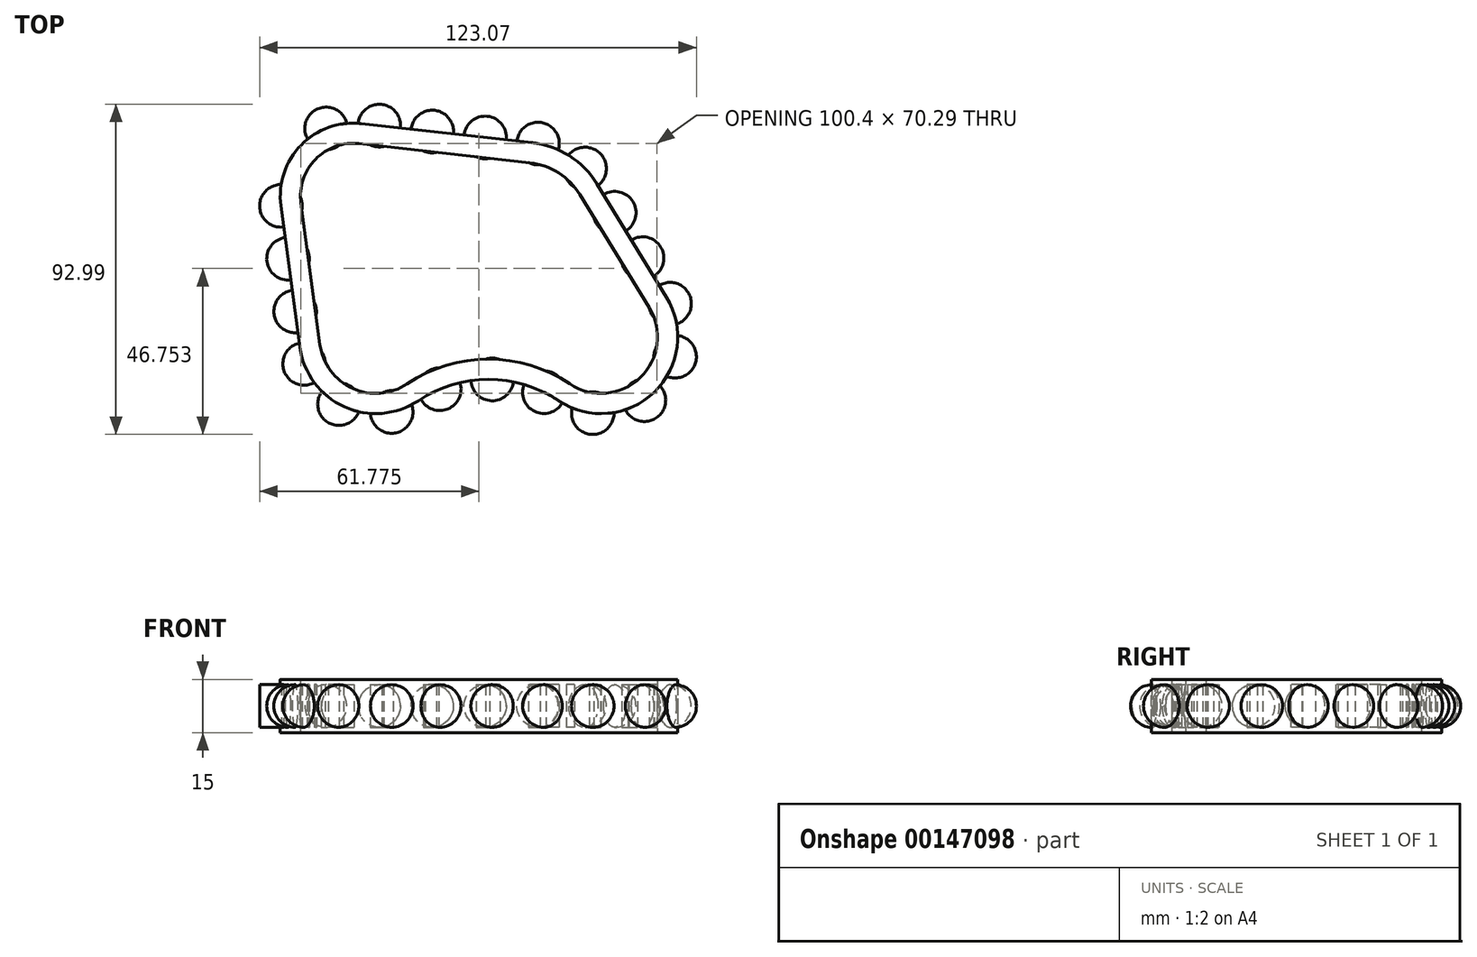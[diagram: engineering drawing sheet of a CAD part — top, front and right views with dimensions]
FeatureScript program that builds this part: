
annotation { "Feature Type Name" : "Feature", "Feature Type Description" : "" }
export const myFeature = defineFeature(function(context is Context, id is Id, definition is map)
    precondition{}
    {
        {
            var Q0;
            Q0=qCreatedBy(makeId("Top.planeOp"),FACE);
            var sketch = newSketch(context, id + "F0", { "sketchPlane" : qUnion([Q0])});
            skArc(sketch, "E0", {"start": v(-47.48, -2.12) * mm, "mid": v(-38.28, -14.47) * mm, "end": v(-22.93, -13.2) * mm});
            skArc(sketch, "E1", {"start": v(22.93, -13.2) * mm, "mid": v(42.76, -11.44) * mm, "end": v(45.28, 8.3) * mm});
            skLineSegment(sketch, "E2", {"start": v(-31.75, 0) * mm, "end": v(0, 0) * mm, "construction": true});
            skLineSegment(sketch, "E3", {"start": v(0, 0) * mm, "end": v(31.75, 0) * mm, "construction": true});
            skCircle(sketch, "E4", {"center": v(-38.1, 39.69) * mm, "radius": 15.91 * mm, "construction": true});
            skLineSegment(sketch, "E5", {"start": v(-38.1, 39.69) * mm, "end": v(0, 39.69) * mm, "construction": true});
            skLineSegment(sketch, "E6", {"start": v(0, 39.69) * mm, "end": v(0, 0) * mm, "construction": true});
            skArc(sketch, "E7.0", {"start": v(-53.12, -2.87) * mm, "mid": v(-40.62, -19.65) * mm, "end": v(-19.77, -17.93) * mm});
            skArc(sketch, "E8.0", {"start": v(19.77, -17.93) * mm, "mid": v(46.7, -15.54) * mm, "end": v(50.13, 11.27) * mm});
            skArc(sketch, "E9", {"start": v(22.93, -13.2) * mm, "mid": v(0, -6.24) * mm, "end": v(-22.93, -13.2) * mm});
            skArc(sketch, "E10", {"start": v(19.77, -17.93) * mm, "mid": v(0, -11.93) * mm, "end": v(-19.77, -17.93) * mm});
            skArc(sketch, "E11.0", {"start": v(-35.82, 60.12) * mm, "mid": v(-52.8, 54.06) * mm, "end": v(-58.48, 36.95) * mm});
            skArc(sketch, "E12.0", {"start": v(-36.45, 54.47) * mm, "mid": v(-48.73, 50.08) * mm, "end": v(-52.84, 37.7) * mm});
            skLineSegment(sketch, "E13", {"start": v(-53.12, -2.87) * mm, "end": v(-58.48, 36.95) * mm});
            skLineSegment(sketch, "E14", {"start": v(-47.48, -2.12) * mm, "end": v(-52.84, 37.7) * mm});
            skLineSegment(sketch, "E15.trimOffspring", {"start": v(-36.45, 54.47) * mm, "end": v(11.64, 49.1) * mm});
            skLineSegment(sketch, "E16.trimOffspring", {"start": v(25.76, 40.12) * mm, "end": v(45.28, 8.3) * mm});
            skLineSegment(sketch, "E17.trimOffspring", {"start": v(30.61, 43.1) * mm, "end": v(50.13, 11.27) * mm});
            skLineSegment(sketch, "E18", {"start": v(-35.82, 60.12) * mm, "end": v(12.27, 54.75) * mm});
            skArc(sketch, "E19.trimOffspring", {"start": v(25.76, 40.12) * mm, "mid": v(19.74, 46.24) * mm, "end": v(11.64, 49.1) * mm});
            skArc(sketch, "E20.trimOffspring", {"start": v(30.61, 43.1) * mm, "mid": v(22.8, 51.04) * mm, "end": v(12.27, 54.75) * mm});
            skLineSegment(sketch, "E21.0", {"start": v(-36.34, 55.46) * mm, "end": v(11.75, 50.09) * mm, "construction": true});
            skArc(sketch, "E21.1", {"start": v(26.62, 40.65) * mm, "mid": v(20.28, 47.09) * mm, "end": v(11.75, 50.09) * mm, "construction": true});
            skArc(sketch, "E21.2", {"start": v(-36.34, 55.46) * mm, "mid": v(-49.45, 50.78) * mm, "end": v(-53.83, 37.57) * mm, "construction": true});
            skLineSegment(sketch, "E21.3", {"start": v(26.62, 40.65) * mm, "end": v(46.13, 8.82) * mm, "construction": true});
            skLineSegment(sketch, "E21.4", {"start": v(-48.47, -2.25) * mm, "end": v(-53.83, 37.57) * mm, "construction": true});
            skArc(sketch, "E21.5", {"start": v(-48.47, -2.25) * mm, "mid": v(-38.7, -15.38) * mm, "end": v(-22.38, -14.03) * mm, "construction": true});
            skArc(sketch, "E21.6", {"start": v(22.37, -14.03) * mm, "mid": v(0, -7.24) * mm, "end": v(-22.38, -14.03) * mm, "construction": true});
            skArc(sketch, "E21.7", {"start": v(22.37, -14.03) * mm, "mid": v(43.45, -12.16) * mm, "end": v(46.13, 8.82) * mm, "construction": true});
            skPoint(sketch, "E22.trimOffspring.end.orphan", {"position": v(38.1, 39.69) * mm});
            skSolve(sketch);
        }
        {
            var Q0;
            Q0=makeQuery(id+"F0.imprint","IMPRINT",FACE,{"disambiguationData":[TD([[makeQuery(id+"F0.imprint","IMPRINT",EDGE,{"derivedFrom":sQuery(id+"F0.wireOp",EDGE,"E0")}),-1.0]])]});
            extrude(context, id + "F1", {"entities" : qUnion([Q0]), "depth" : 15 * mm});
        }
        {
            var Q0;
            Q0=makeQuery(id+"F1.opExtrude","CAP_FACE",FACE,{"disambiguationData":[OSD([sQuery(id+"F0.wireOp",EDGE,"E0"),sQuery(id+"F0.wireOp",EDGE,"E1"),sQuery(id+"F0.wireOp",EDGE,"E7.0"),sQuery(id+"F0.wireOp",EDGE,"E8.0"),sQuery(id+"F0.wireOp",EDGE,"E9"),sQuery(id+"F0.wireOp",EDGE,"E10"),sQuery(id+"F0.wireOp",EDGE,"E11.0"),sQuery(id+"F0.wireOp",EDGE,"E12.0"),sQuery(id+"F0.wireOp",EDGE,"E13"),sQuery(id+"F0.wireOp",EDGE,"YvZVE2Dw-0EEV-0Uc5-rsGK-UycfFpxis624"),sQuery(id+"F0.wireOp",EDGE,"E14"),sQuery(id+"F0.wireOp",EDGE,"E15.trimOffspring")])],"isStart":false});
            var Q1;
            Q1=makeQuery(id+"F1.opExtrude","CAP_FACE",FACE,{"disambiguationData":[OSD([sQuery(id+"F0.wireOp",EDGE,"E0"),sQuery(id+"F0.wireOp",EDGE,"E1"),sQuery(id+"F0.wireOp",EDGE,"E7.0"),sQuery(id+"F0.wireOp",EDGE,"E8.0"),sQuery(id+"F0.wireOp",EDGE,"E9"),sQuery(id+"F0.wireOp",EDGE,"E10"),sQuery(id+"F0.wireOp",EDGE,"E11.0"),sQuery(id+"F0.wireOp",EDGE,"E12.0"),sQuery(id+"F0.wireOp",EDGE,"E13"),sQuery(id+"F0.wireOp",EDGE,"YvZVE2Dw-0EEV-0Uc5-rsGK-UycfFpxis624"),sQuery(id+"F0.wireOp",EDGE,"E14"),sQuery(id+"F0.wireOp",EDGE,"E15.trimOffspring")])],"isStart":true});
            cPlane(context, id + "F2", {"entities" : qUnion([Q0, Q1]), "cplaneType" : CPlaneType.MID_PLANE, "offset" : 25.4 * mm, "width" : 152.4 * mm, "height" : 152.4 * mm});
        }
        {
            var Q0;
            Q0=qCreatedBy(id+"F2.planeOp",FACE);
            var sketch = newSketch(context, id + "F3", { "sketchPlane" : qUnion([Q0])});
            skArc(sketch, "E23", {"start": v(-35.82, 60.12) * mm, "mid": v(-52.8, 54.06) * mm, "end": v(-58.48, 36.95) * mm, "construction": true});
            skArc(sketch, "E24", {"start": v(-53.12, -2.87) * mm, "mid": v(-40.62, -19.65) * mm, "end": v(-19.77, -17.93) * mm, "construction": true});
            skArc(sketch, "E25", {"start": v(19.77, -17.93) * mm, "mid": v(0, -11.93) * mm, "end": v(-19.77, -17.93) * mm, "construction": true});
            skArc(sketch, "E26", {"start": v(19.77, -17.93) * mm, "mid": v(46.7, -15.54) * mm, "end": v(50.13, 11.27) * mm, "construction": true});
            skArc(sketch, "E27", {"start": v(30.61, 43.1) * mm, "mid": v(22.8, 51.04) * mm, "end": v(12.27, 54.75) * mm, "construction": true});
            skLineSegment(sketch, "E28", {"start": v(-35.82, 60.12) * mm, "end": v(12.27, 54.75) * mm, "construction": true});
            skLineSegment(sketch, "E29", {"start": v(30.61, 43.1) * mm, "end": v(50.13, 11.27) * mm, "construction": true});
            skLineSegment(sketch, "E30", {"start": v(-53.12, -2.87) * mm, "end": v(-58.48, 36.95) * mm, "construction": true});
            skCircle(sketch, "E31", {"center": v(35.57, 35.02) * mm, "radius": 6 * mm});
            skCircle(sketch, "E32", {"center": v(43.41, 22.23) * mm, "radius": 6 * mm});
            skCircle(sketch, "E33", {"center": v(51.16, 9.39) * mm, "radius": 6 * mm});
            skCircle(sketch, "E34", {"center": v(52.6, -5.54) * mm, "radius": 6 * mm});
            skCircle(sketch, "E35", {"center": v(43.93, -17.8) * mm, "radius": 6 * mm});
            skCircle(sketch, "E36", {"center": v(29.38, -21.43) * mm, "radius": 6 * mm});
            skCircle(sketch, "E37", {"center": v(15.6, -15.53) * mm, "radius": 6 * mm});
            skCircle(sketch, "E38", {"center": v(1.03, -11.95) * mm, "radius": 6 * mm});
            skCircle(sketch, "E39", {"center": v(-13.72, -14.69) * mm, "radius": 6 * mm});
            skCircle(sketch, "E40", {"center": v(-27.28, -21.1) * mm, "radius": 6 * mm});
            skCircle(sketch, "E41", {"center": v(-42.12, -18.9) * mm, "radius": 6 * mm});
            skCircle(sketch, "E42", {"center": v(-51.94, -7.57) * mm, "radius": 6 * mm});
            skCircle(sketch, "E43", {"center": v(-54.48, 7.21) * mm, "radius": 6 * mm});
            skCircle(sketch, "E44", {"center": v(-56.48, 22.08) * mm, "radius": 6 * mm});
            skCircle(sketch, "E45", {"center": v(-58.48, 36.95) * mm, "radius": 6 * mm});
            skCircle(sketch, "E46", {"center": v(-45.76, 58.77) * mm, "radius": 6 * mm});
            skCircle(sketch, "E47", {"center": v(-30.76, 59.56) * mm, "radius": 6 * mm});
            skCircle(sketch, "E48", {"center": v(-15.85, 57.9) * mm, "radius": 6 * mm});
            skCircle(sketch, "E49", {"center": v(-0.95, 56.23) * mm, "radius": 6 * mm});
            skCircle(sketch, "E50", {"center": v(13.95, 54.5) * mm, "radius": 6 * mm});
            skCircle(sketch, "E51", {"center": v(27.2, 47.47) * mm, "radius": 6 * mm});
            skLineSegment(sketch, "E52", {"start": v(-58.48, 36.95) * mm, "end": v(-56.48, 22.08) * mm, "construction": true});
            skLineSegment(sketch, "E53", {"start": v(-56.48, 22.08) * mm, "end": v(-54.48, 7.21) * mm, "construction": true});
            skLineSegment(sketch, "E54", {"start": v(-54.48, 7.21) * mm, "end": v(-51.94, -7.57) * mm, "construction": true});
            skLineSegment(sketch, "E55", {"start": v(-51.94, -7.57) * mm, "end": v(-42.12, -18.9) * mm, "construction": true});
            skLineSegment(sketch, "E56", {"start": v(-42.12, -18.9) * mm, "end": v(-27.28, -21.1) * mm, "construction": true});
            skLineSegment(sketch, "E57", {"start": v(-27.28, -21.1) * mm, "end": v(-13.72, -14.69) * mm, "construction": true});
            skLineSegment(sketch, "E58", {"start": v(-13.72, -14.69) * mm, "end": v(1.03, -11.95) * mm, "construction": true});
            skLineSegment(sketch, "E59", {"start": v(1.03, -11.95) * mm, "end": v(15.6, -15.53) * mm, "construction": true});
            skLineSegment(sketch, "E60", {"start": v(15.6, -15.53) * mm, "end": v(16.69, -16.09) * mm, "construction": true});
            skLineSegment(sketch, "E61", {"start": v(29.38, -21.43) * mm, "end": v(43.93, -17.8) * mm, "construction": true});
            skLineSegment(sketch, "E62", {"start": v(43.93, -17.8) * mm, "end": v(52.6, -5.54) * mm, "construction": true});
            skLineSegment(sketch, "E63", {"start": v(52.6, -5.54) * mm, "end": v(51.16, 9.39) * mm, "construction": true});
            skLineSegment(sketch, "E64", {"start": v(51.16, 9.39) * mm, "end": v(43.41, 22.23) * mm, "construction": true});
            skLineSegment(sketch, "E65", {"start": v(43.41, 22.23) * mm, "end": v(35.57, 35.02) * mm, "construction": true});
            skLineSegment(sketch, "E66", {"start": v(35.57, 35.02) * mm, "end": v(27.2, 47.47) * mm, "construction": true});
            skLineSegment(sketch, "E67", {"start": v(27.2, 47.47) * mm, "end": v(13.95, 54.5) * mm, "construction": true});
            skLineSegment(sketch, "E68", {"start": v(13.95, 54.5) * mm, "end": v(-0.95, 56.23) * mm, "construction": true});
            skLineSegment(sketch, "E69", {"start": v(-0.95, 56.23) * mm, "end": v(-15.85, 57.9) * mm, "construction": true});
            skLineSegment(sketch, "E70", {"start": v(-15.85, 57.9) * mm, "end": v(-30.76, 59.56) * mm, "construction": true});
            skLineSegment(sketch, "E71", {"start": v(-45.76, 58.77) * mm, "end": v(-56.68, 48.49) * mm, "construction": true});
            skLineSegment(sketch, "E72", {"start": v(15.6, -15.53) * mm, "end": v(29.38, -21.43) * mm, "construction": true});
            skSolve(sketch);
        }
        {
            var Q0;
            {var subQ0=sQuery(id+"F3.wireOp",EDGE,"Tip8s4cw-0h8X-FGlb-H3H5-F3ooNThYM5mk");var subQ1=sQuery(id+"F3.wireOp",EDGE,"E45");var subQ2=makeQuery(id+"F3.imprint","INTERSECT",VERTEX,{"disambiguationData":[OD(0.0)],"derivedFrom":[subQ1,subQ0]});Q0=makeQuery(id+"F3.imprint","IMPRINT",FACE,{"disambiguationData":[TD([[makeQuery(id+"F3.imprint","IMPRINT",EDGE,{"disambiguationData":[TD([[subQ2,1.0]])],"derivedFrom":subQ1}),-1.0]])]});}
            var Q1;
            {var subQ0=sQuery(id+"F3.wireOp",EDGE,"Tip8s4cw-0h8X-FGlb-H3H5-F3ooNThYM5mk");var subQ1=sQuery(id+"F3.wireOp",EDGE,"E45");var subQ2=makeQuery(id+"F3.imprint","INTERSECT",VERTEX,{"disambiguationData":[OD(0.0)],"derivedFrom":[subQ1,subQ0]});Q1=makeQuery(id+"F3.imprint","IMPRINT",FACE,{"disambiguationData":[TD([[makeQuery(id+"F3.imprint","IMPRINT",EDGE,{"disambiguationData":[TD([[subQ2,-1.0]])],"derivedFrom":subQ1}),1.0]])]});}
            var Q2;
            Q2=makeQuery(id+"F3.imprint","IMPRINT",FACE,{"disambiguationData":[TD([[makeQuery(id+"F3.imprint","IMPRINT",EDGE,{"derivedFrom":sQuery(id+"F3.wireOp",EDGE,"E44")}),1.0]])]});
            var Q3;
            Q3=makeQuery(id+"F3.imprint","IMPRINT",FACE,{"disambiguationData":[TD([[makeQuery(id+"F3.imprint","IMPRINT",EDGE,{"derivedFrom":sQuery(id+"F3.wireOp",EDGE,"E43")}),1.0]])]});
            var Q4;
            Q4=makeQuery(id+"F3.imprint","IMPRINT",FACE,{"disambiguationData":[TD([[makeQuery(id+"F3.imprint","IMPRINT",EDGE,{"derivedFrom":sQuery(id+"F3.wireOp",EDGE,"E42")}),1.0]])]});
            var Q5;
            Q5=makeQuery(id+"F3.imprint","IMPRINT",FACE,{"disambiguationData":[TD([[makeQuery(id+"F3.imprint","IMPRINT",EDGE,{"derivedFrom":sQuery(id+"F3.wireOp",EDGE,"E41")}),1.0]])]});
            var Q6;
            Q6=makeQuery(id+"F3.imprint","IMPRINT",FACE,{"disambiguationData":[TD([[makeQuery(id+"F3.imprint","IMPRINT",EDGE,{"derivedFrom":sQuery(id+"F3.wireOp",EDGE,"E40")}),1.0]])]});
            var Q7;
            Q7=makeQuery(id+"F3.imprint","IMPRINT",FACE,{"disambiguationData":[TD([[makeQuery(id+"F3.imprint","IMPRINT",EDGE,{"derivedFrom":sQuery(id+"F3.wireOp",EDGE,"E39")}),1.0]])]});
            var Q8;
            Q8=makeQuery(id+"F3.imprint","IMPRINT",FACE,{"disambiguationData":[TD([[makeQuery(id+"F3.imprint","IMPRINT",EDGE,{"derivedFrom":sQuery(id+"F3.wireOp",EDGE,"E38")}),1.0]])]});
            var Q9;
            Q9=makeQuery(id+"F3.imprint","IMPRINT",FACE,{"disambiguationData":[TD([[makeQuery(id+"F3.imprint","IMPRINT",EDGE,{"derivedFrom":sQuery(id+"F3.wireOp",EDGE,"E37")}),1.0]])]});
            var Q10;
            Q10=makeQuery(id+"F3.imprint","IMPRINT",FACE,{"disambiguationData":[TD([[makeQuery(id+"F3.imprint","IMPRINT",EDGE,{"derivedFrom":sQuery(id+"F3.wireOp",EDGE,"E36")}),1.0]])]});
            var Q11;
            Q11=makeQuery(id+"F3.imprint","IMPRINT",FACE,{"disambiguationData":[TD([[makeQuery(id+"F3.imprint","IMPRINT",EDGE,{"derivedFrom":sQuery(id+"F3.wireOp",EDGE,"E35")}),1.0]])]});
            var Q12;
            Q12=makeQuery(id+"F3.imprint","IMPRINT",FACE,{"disambiguationData":[TD([[makeQuery(id+"F3.imprint","IMPRINT",EDGE,{"derivedFrom":sQuery(id+"F3.wireOp",EDGE,"E34")}),1.0]])]});
            var Q13;
            Q13=makeQuery(id+"F3.imprint","IMPRINT",FACE,{"disambiguationData":[TD([[makeQuery(id+"F3.imprint","IMPRINT",EDGE,{"derivedFrom":sQuery(id+"F3.wireOp",EDGE,"E33")}),1.0]])]});
            var Q14;
            Q14=makeQuery(id+"F3.imprint","IMPRINT",FACE,{"disambiguationData":[TD([[makeQuery(id+"F3.imprint","IMPRINT",EDGE,{"derivedFrom":sQuery(id+"F3.wireOp",EDGE,"E32")}),1.0]])]});
            var Q15;
            Q15=makeQuery(id+"F3.imprint","IMPRINT",FACE,{"disambiguationData":[TD([[makeQuery(id+"F3.imprint","IMPRINT",EDGE,{"derivedFrom":sQuery(id+"F3.wireOp",EDGE,"E31")}),1.0]])]});
            var Q16;
            Q16=makeQuery(id+"F3.imprint","IMPRINT",FACE,{"disambiguationData":[TD([[makeQuery(id+"F3.imprint","IMPRINT",EDGE,{"derivedFrom":sQuery(id+"F3.wireOp",EDGE,"E51")}),1.0]])]});
            var Q17;
            Q17=makeQuery(id+"F3.imprint","IMPRINT",FACE,{"disambiguationData":[TD([[makeQuery(id+"F3.imprint","IMPRINT",EDGE,{"derivedFrom":sQuery(id+"F3.wireOp",EDGE,"E50")}),1.0]])]});
            var Q18;
            Q18=makeQuery(id+"F3.imprint","IMPRINT",FACE,{"disambiguationData":[TD([[makeQuery(id+"F3.imprint","IMPRINT",EDGE,{"derivedFrom":sQuery(id+"F3.wireOp",EDGE,"E49")}),1.0]])]});
            var Q19;
            Q19=makeQuery(id+"F3.imprint","IMPRINT",FACE,{"disambiguationData":[TD([[makeQuery(id+"F3.imprint","IMPRINT",EDGE,{"derivedFrom":sQuery(id+"F3.wireOp",EDGE,"E48")}),1.0]])]});
            var Q20;
            Q20=makeQuery(id+"F3.imprint","IMPRINT",FACE,{"disambiguationData":[TD([[makeQuery(id+"F3.imprint","IMPRINT",EDGE,{"derivedFrom":sQuery(id+"F3.wireOp",EDGE,"E47")}),1.0]])]});
            var Q21;
            Q21=makeQuery(id+"F3.imprint","IMPRINT",FACE,{"disambiguationData":[TD([[makeQuery(id+"F3.imprint","IMPRINT",EDGE,{"derivedFrom":sQuery(id+"F3.wireOp",EDGE,"E46")}),1.0]])]});
            extrude(context, id + "F4", {"entities" : qUnion([Q0, Q1, Q2, Q3, Q4, Q5, Q6, Q7, Q8, Q9, Q10, Q11, Q12, Q13, Q14, Q15, Q16, Q17, Q18, Q19, Q20, Q21]), "operationType" : NewBodyOperationType.ADD, "endBound" : BoundingType.SYMMETRIC, "depth" : 12 * mm});
        }
        {
            var Q0;
            {var subQ0=sQuery(id+"F3.wireOp",EDGE,"E44");Q0=makeQuery(id+"F4.boolean.opBoolean","SPLIT",EDGE,{"disambiguationData":[TD([makeQuery(id+"F1.opExtrude","SWEPT_FACE",FACE,{"disambiguationData":[OSD([sQuery(id+"F0.wireOp",EDGE,"E13")])]})])],"derivedFrom":makeQuery(id+"F4.opExtrude","CAP_EDGE",EDGE,{"disambiguationData":[OSD([subQ0])],"isStart":false})});}
            var Q1;
            {var subQ0=sQuery(id+"F3.wireOp",EDGE,"E44");Q1=makeQuery(id+"F4.boolean.opBoolean","SPLIT",EDGE,{"disambiguationData":[TD([makeQuery(id+"F1.opExtrude","SWEPT_FACE",FACE,{"disambiguationData":[OSD([sQuery(id+"F0.wireOp",EDGE,"E13")])]})])],"derivedFrom":makeQuery(id+"F4.opExtrude","CAP_EDGE",EDGE,{"disambiguationData":[OSD([subQ0])],"isStart":true})});}
            var Q2;
            {var subQ0=sQuery(id+"F3.wireOp",EDGE,"E43");Q2=makeQuery(id+"F4.boolean.opBoolean","SPLIT",EDGE,{"disambiguationData":[TD([makeQuery(id+"F1.opExtrude","SWEPT_FACE",FACE,{"disambiguationData":[OSD([sQuery(id+"F0.wireOp",EDGE,"E13")])]})])],"derivedFrom":makeQuery(id+"F4.opExtrude","CAP_EDGE",EDGE,{"disambiguationData":[OSD([subQ0])],"isStart":true})});}
            var Q3;
            {var subQ0=sQuery(id+"F3.wireOp",EDGE,"E43");Q3=makeQuery(id+"F4.boolean.opBoolean","SPLIT",EDGE,{"disambiguationData":[TD([makeQuery(id+"F1.opExtrude","SWEPT_FACE",FACE,{"disambiguationData":[OSD([sQuery(id+"F0.wireOp",EDGE,"E13")])]})])],"derivedFrom":makeQuery(id+"F4.opExtrude","CAP_EDGE",EDGE,{"disambiguationData":[OSD([subQ0])],"isStart":false})});}
            var Q4;
            {var subQ0=sQuery(id+"F3.wireOp",EDGE,"E42");Q4=makeQuery(id+"F4.boolean.opBoolean","SPLIT",EDGE,{"disambiguationData":[TD([makeQuery(id+"F1.opExtrude","SWEPT_FACE",FACE,{"disambiguationData":[OSD([sQuery(id+"F0.wireOp",EDGE,"E7.0")])]})])],"derivedFrom":makeQuery(id+"F4.opExtrude","CAP_EDGE",EDGE,{"disambiguationData":[OSD([subQ0])],"isStart":false})});}
            var Q5;
            {var subQ0=sQuery(id+"F3.wireOp",EDGE,"E42");Q5=makeQuery(id+"F4.boolean.opBoolean","SPLIT",EDGE,{"disambiguationData":[TD([makeQuery(id+"F1.opExtrude","SWEPT_FACE",FACE,{"disambiguationData":[OSD([sQuery(id+"F0.wireOp",EDGE,"E7.0")])]})])],"derivedFrom":makeQuery(id+"F4.opExtrude","CAP_EDGE",EDGE,{"disambiguationData":[OSD([subQ0])],"isStart":true})});}
            var Q6;
            {var subQ0=sQuery(id+"F3.wireOp",EDGE,"E41");Q6=makeQuery(id+"F4.boolean.opBoolean","SPLIT",EDGE,{"disambiguationData":[TD([makeQuery(id+"F1.opExtrude","SWEPT_FACE",FACE,{"disambiguationData":[OSD([sQuery(id+"F0.wireOp",EDGE,"E7.0")])]})])],"derivedFrom":makeQuery(id+"F4.opExtrude","CAP_EDGE",EDGE,{"disambiguationData":[OSD([subQ0])],"isStart":true})});}
            var Q7;
            {var subQ0=sQuery(id+"F3.wireOp",EDGE,"E41");Q7=makeQuery(id+"F4.boolean.opBoolean","SPLIT",EDGE,{"disambiguationData":[TD([makeQuery(id+"F1.opExtrude","SWEPT_FACE",FACE,{"disambiguationData":[OSD([sQuery(id+"F0.wireOp",EDGE,"E7.0")])]})])],"derivedFrom":makeQuery(id+"F4.opExtrude","CAP_EDGE",EDGE,{"disambiguationData":[OSD([subQ0])],"isStart":false})});}
            var Q8;
            {var subQ0=sQuery(id+"F3.wireOp",EDGE,"E40");Q8=makeQuery(id+"F4.boolean.opBoolean","SPLIT",EDGE,{"disambiguationData":[TD([makeQuery(id+"F1.opExtrude","SWEPT_FACE",FACE,{"disambiguationData":[OSD([sQuery(id+"F0.wireOp",EDGE,"E7.0")])]})])],"derivedFrom":makeQuery(id+"F4.opExtrude","CAP_EDGE",EDGE,{"disambiguationData":[OSD([subQ0])],"isStart":false})});}
            var Q9;
            {var subQ0=sQuery(id+"F3.wireOp",EDGE,"E40");Q9=makeQuery(id+"F4.boolean.opBoolean","SPLIT",EDGE,{"disambiguationData":[TD([makeQuery(id+"F1.opExtrude","SWEPT_FACE",FACE,{"disambiguationData":[OSD([sQuery(id+"F0.wireOp",EDGE,"E7.0")])]})])],"derivedFrom":makeQuery(id+"F4.opExtrude","CAP_EDGE",EDGE,{"disambiguationData":[OSD([subQ0])],"isStart":true})});}
            var Q10;
            {var subQ0=sQuery(id+"F3.wireOp",EDGE,"E39");Q10=makeQuery(id+"F4.boolean.opBoolean","SPLIT",EDGE,{"disambiguationData":[TD([makeQuery(id+"F1.opExtrude","SWEPT_FACE",FACE,{"disambiguationData":[OSD([sQuery(id+"F0.wireOp",EDGE,"E10")])]})])],"derivedFrom":makeQuery(id+"F4.opExtrude","CAP_EDGE",EDGE,{"disambiguationData":[OSD([subQ0])],"isStart":true})});}
            var Q11;
            {var subQ0=sQuery(id+"F3.wireOp",EDGE,"E38");Q11=makeQuery(id+"F4.boolean.opBoolean","SPLIT",EDGE,{"disambiguationData":[TD([makeQuery(id+"F1.opExtrude","SWEPT_FACE",FACE,{"disambiguationData":[OSD([sQuery(id+"F0.wireOp",EDGE,"E10")])]})])],"derivedFrom":makeQuery(id+"F4.opExtrude","CAP_EDGE",EDGE,{"disambiguationData":[OSD([subQ0])],"isStart":true})});}
            var Q12;
            {var subQ0=sQuery(id+"F3.wireOp",EDGE,"E38");Q12=makeQuery(id+"F4.boolean.opBoolean","SPLIT",EDGE,{"disambiguationData":[TD([makeQuery(id+"F1.opExtrude","SWEPT_FACE",FACE,{"disambiguationData":[OSD([sQuery(id+"F0.wireOp",EDGE,"E10")])]})])],"derivedFrom":makeQuery(id+"F4.opExtrude","CAP_EDGE",EDGE,{"disambiguationData":[OSD([subQ0])],"isStart":false})});}
            var Q13;
            {var subQ0=sQuery(id+"F3.wireOp",EDGE,"E37");Q13=makeQuery(id+"F4.boolean.opBoolean","SPLIT",EDGE,{"disambiguationData":[TD([makeQuery(id+"F1.opExtrude","SWEPT_FACE",FACE,{"disambiguationData":[OSD([sQuery(id+"F0.wireOp",EDGE,"E8.0")])]})])],"derivedFrom":makeQuery(id+"F4.opExtrude","CAP_EDGE",EDGE,{"disambiguationData":[OSD([subQ0])],"isStart":true})});}
            var Q14;
            {var subQ0=sQuery(id+"F3.wireOp",EDGE,"E37");Q14=makeQuery(id+"F4.boolean.opBoolean","SPLIT",EDGE,{"disambiguationData":[TD([makeQuery(id+"F1.opExtrude","SWEPT_FACE",FACE,{"disambiguationData":[OSD([sQuery(id+"F0.wireOp",EDGE,"E8.0")])]})])],"derivedFrom":makeQuery(id+"F4.opExtrude","CAP_EDGE",EDGE,{"disambiguationData":[OSD([subQ0])],"isStart":false})});}
            var Q15;
            {var subQ0=sQuery(id+"F3.wireOp",EDGE,"E36");Q15=makeQuery(id+"F4.boolean.opBoolean","SPLIT",EDGE,{"disambiguationData":[TD([makeQuery(id+"F1.opExtrude","SWEPT_FACE",FACE,{"disambiguationData":[OSD([sQuery(id+"F0.wireOp",EDGE,"E8.0")])]})])],"derivedFrom":makeQuery(id+"F4.opExtrude","CAP_EDGE",EDGE,{"disambiguationData":[OSD([subQ0])],"isStart":false})});}
            var Q16;
            {var subQ0=sQuery(id+"F3.wireOp",EDGE,"E36");Q16=makeQuery(id+"F4.boolean.opBoolean","SPLIT",EDGE,{"disambiguationData":[TD([makeQuery(id+"F1.opExtrude","SWEPT_FACE",FACE,{"disambiguationData":[OSD([sQuery(id+"F0.wireOp",EDGE,"E8.0")])]})])],"derivedFrom":makeQuery(id+"F4.opExtrude","CAP_EDGE",EDGE,{"disambiguationData":[OSD([subQ0])],"isStart":true})});}
            var Q17;
            {var subQ0=sQuery(id+"F3.wireOp",EDGE,"E35");Q17=makeQuery(id+"F4.boolean.opBoolean","SPLIT",EDGE,{"disambiguationData":[TD([makeQuery(id+"F1.opExtrude","SWEPT_FACE",FACE,{"disambiguationData":[OSD([sQuery(id+"F0.wireOp",EDGE,"E8.0")])]})])],"derivedFrom":makeQuery(id+"F4.opExtrude","CAP_EDGE",EDGE,{"disambiguationData":[OSD([subQ0])],"isStart":true})});}
            var Q18;
            {var subQ0=sQuery(id+"F3.wireOp",EDGE,"E34");Q18=makeQuery(id+"F4.boolean.opBoolean","SPLIT",EDGE,{"disambiguationData":[TD([makeQuery(id+"F1.opExtrude","SWEPT_FACE",FACE,{"disambiguationData":[OSD([sQuery(id+"F0.wireOp",EDGE,"E8.0")])]})])],"derivedFrom":makeQuery(id+"F4.opExtrude","CAP_EDGE",EDGE,{"disambiguationData":[OSD([subQ0])],"isStart":true})});}
            var Q19;
            {var subQ0=sQuery(id+"F3.wireOp",EDGE,"E34");Q19=makeQuery(id+"F4.boolean.opBoolean","SPLIT",EDGE,{"disambiguationData":[TD([makeQuery(id+"F1.opExtrude","SWEPT_FACE",FACE,{"disambiguationData":[OSD([sQuery(id+"F0.wireOp",EDGE,"E8.0")])]})])],"derivedFrom":makeQuery(id+"F4.opExtrude","CAP_EDGE",EDGE,{"disambiguationData":[OSD([subQ0])],"isStart":false})});}
            var Q20;
            {var subQ0=sQuery(id+"F3.wireOp",EDGE,"E35");Q20=makeQuery(id+"F4.boolean.opBoolean","SPLIT",EDGE,{"disambiguationData":[TD([makeQuery(id+"F1.opExtrude","SWEPT_FACE",FACE,{"disambiguationData":[OSD([sQuery(id+"F0.wireOp",EDGE,"E8.0")])]})])],"derivedFrom":makeQuery(id+"F4.opExtrude","CAP_EDGE",EDGE,{"disambiguationData":[OSD([subQ0])],"isStart":false})});}
            var Q21;
            {var subQ0=sQuery(id+"F3.wireOp",EDGE,"E33");Q21=makeQuery(id+"F4.boolean.opBoolean","SPLIT",EDGE,{"disambiguationData":[TD([makeQuery(id+"F1.opExtrude","SWEPT_FACE",FACE,{"disambiguationData":[OSD([sQuery(id+"F0.wireOp",EDGE,"E8.0")])]})])],"derivedFrom":makeQuery(id+"F4.opExtrude","CAP_EDGE",EDGE,{"disambiguationData":[OSD([subQ0])],"isStart":false})});}
            var Q22;
            {var subQ0=sQuery(id+"F3.wireOp",EDGE,"E33");Q22=makeQuery(id+"F4.boolean.opBoolean","SPLIT",EDGE,{"disambiguationData":[TD([makeQuery(id+"F1.opExtrude","SWEPT_FACE",FACE,{"disambiguationData":[OSD([sQuery(id+"F0.wireOp",EDGE,"E8.0")])]})])],"derivedFrom":makeQuery(id+"F4.opExtrude","CAP_EDGE",EDGE,{"disambiguationData":[OSD([subQ0])],"isStart":true})});}
            var Q23;
            {var subQ0=sQuery(id+"F3.wireOp",EDGE,"E32");Q23=makeQuery(id+"F4.boolean.opBoolean","SPLIT",EDGE,{"disambiguationData":[TD([makeQuery(id+"F1.opExtrude","SWEPT_FACE",FACE,{"disambiguationData":[OSD([sQuery(id+"F0.wireOp",EDGE,"E17.trimOffspring")])]})])],"derivedFrom":makeQuery(id+"F4.opExtrude","CAP_EDGE",EDGE,{"disambiguationData":[OSD([subQ0])],"isStart":false})});}
            var Q24;
            {var subQ0=sQuery(id+"F3.wireOp",EDGE,"E32");Q24=makeQuery(id+"F4.boolean.opBoolean","SPLIT",EDGE,{"disambiguationData":[TD([makeQuery(id+"F1.opExtrude","SWEPT_FACE",FACE,{"disambiguationData":[OSD([sQuery(id+"F0.wireOp",EDGE,"E17.trimOffspring")])]})])],"derivedFrom":makeQuery(id+"F4.opExtrude","CAP_EDGE",EDGE,{"disambiguationData":[OSD([subQ0])],"isStart":true})});}
            var Q25;
            {var subQ0=sQuery(id+"F3.wireOp",EDGE,"E31");Q25=makeQuery(id+"F4.boolean.opBoolean","SPLIT",EDGE,{"disambiguationData":[TD([makeQuery(id+"F1.opExtrude","SWEPT_FACE",FACE,{"disambiguationData":[OSD([sQuery(id+"F0.wireOp",EDGE,"E17.trimOffspring")])]})])],"derivedFrom":makeQuery(id+"F4.opExtrude","CAP_EDGE",EDGE,{"disambiguationData":[OSD([subQ0])],"isStart":false})});}
            var Q26;
            {var subQ0=sQuery(id+"F3.wireOp",EDGE,"E31");Q26=makeQuery(id+"F4.boolean.opBoolean","SPLIT",EDGE,{"disambiguationData":[TD([makeQuery(id+"F1.opExtrude","SWEPT_FACE",FACE,{"disambiguationData":[OSD([sQuery(id+"F0.wireOp",EDGE,"E17.trimOffspring")])]})])],"derivedFrom":makeQuery(id+"F4.opExtrude","CAP_EDGE",EDGE,{"disambiguationData":[OSD([subQ0])],"isStart":true})});}
            var Q27;
            {var subQ0=sQuery(id+"F3.wireOp",EDGE,"E51");Q27=makeQuery(id+"F4.boolean.opBoolean","SPLIT",EDGE,{"disambiguationData":[TD([makeQuery(id+"F1.opExtrude","SWEPT_FACE",FACE,{"disambiguationData":[OSD([sQuery(id+"F0.wireOp",EDGE,"E17.trimOffspring")])]})])],"derivedFrom":makeQuery(id+"F4.opExtrude","CAP_EDGE",EDGE,{"disambiguationData":[OSD([subQ0])],"isStart":false})});}
            var Q28;
            {var subQ0=sQuery(id+"F3.wireOp",EDGE,"E50");Q28=makeQuery(id+"F4.boolean.opBoolean","SPLIT",EDGE,{"disambiguationData":[TD([makeQuery(id+"F1.opExtrude","SWEPT_FACE",FACE,{"disambiguationData":[OSD([sQuery(id+"F0.wireOp",EDGE,"E18")])]})])],"derivedFrom":makeQuery(id+"F4.opExtrude","CAP_EDGE",EDGE,{"disambiguationData":[OSD([subQ0])],"isStart":true})});}
            var Q29;
            {var subQ0=sQuery(id+"F3.wireOp",EDGE,"E51");Q29=makeQuery(id+"F4.boolean.opBoolean","SPLIT",EDGE,{"disambiguationData":[TD([makeQuery(id+"F1.opExtrude","SWEPT_FACE",FACE,{"disambiguationData":[OSD([sQuery(id+"F0.wireOp",EDGE,"E17.trimOffspring")])]})])],"derivedFrom":makeQuery(id+"F4.opExtrude","CAP_EDGE",EDGE,{"disambiguationData":[OSD([subQ0])],"isStart":true})});}
            var Q30;
            {var subQ0=sQuery(id+"F3.wireOp",EDGE,"E50");Q30=makeQuery(id+"F4.boolean.opBoolean","SPLIT",EDGE,{"disambiguationData":[TD([makeQuery(id+"F1.opExtrude","SWEPT_FACE",FACE,{"disambiguationData":[OSD([sQuery(id+"F0.wireOp",EDGE,"E18")])]})])],"derivedFrom":makeQuery(id+"F4.opExtrude","CAP_EDGE",EDGE,{"disambiguationData":[OSD([subQ0])],"isStart":false})});}
            var Q31;
            {var subQ0=sQuery(id+"F3.wireOp",EDGE,"E49");Q31=makeQuery(id+"F4.boolean.opBoolean","SPLIT",EDGE,{"disambiguationData":[TD([makeQuery(id+"F1.opExtrude","SWEPT_FACE",FACE,{"disambiguationData":[OSD([sQuery(id+"F0.wireOp",EDGE,"E18")])]})])],"derivedFrom":makeQuery(id+"F4.opExtrude","CAP_EDGE",EDGE,{"disambiguationData":[OSD([subQ0])],"isStart":false})});}
            var Q32;
            {var subQ0=sQuery(id+"F3.wireOp",EDGE,"E49");Q32=makeQuery(id+"F4.boolean.opBoolean","SPLIT",EDGE,{"disambiguationData":[TD([makeQuery(id+"F1.opExtrude","SWEPT_FACE",FACE,{"disambiguationData":[OSD([sQuery(id+"F0.wireOp",EDGE,"E18")])]})])],"derivedFrom":makeQuery(id+"F4.opExtrude","CAP_EDGE",EDGE,{"disambiguationData":[OSD([subQ0])],"isStart":true})});}
            var Q33;
            {var subQ0=sQuery(id+"F3.wireOp",EDGE,"E48");Q33=makeQuery(id+"F4.boolean.opBoolean","SPLIT",EDGE,{"disambiguationData":[TD([makeQuery(id+"F1.opExtrude","SWEPT_FACE",FACE,{"disambiguationData":[OSD([sQuery(id+"F0.wireOp",EDGE,"E18")])]})])],"derivedFrom":makeQuery(id+"F4.opExtrude","CAP_EDGE",EDGE,{"disambiguationData":[OSD([subQ0])],"isStart":true})});}
            var Q34;
            {var subQ0=sQuery(id+"F3.wireOp",EDGE,"E48");Q34=makeQuery(id+"F4.boolean.opBoolean","SPLIT",EDGE,{"disambiguationData":[TD([makeQuery(id+"F1.opExtrude","SWEPT_FACE",FACE,{"disambiguationData":[OSD([sQuery(id+"F0.wireOp",EDGE,"E18")])]})])],"derivedFrom":makeQuery(id+"F4.opExtrude","CAP_EDGE",EDGE,{"disambiguationData":[OSD([subQ0])],"isStart":false})});}
            var Q35;
            {var subQ0=sQuery(id+"F3.wireOp",EDGE,"E47");Q35=makeQuery(id+"F4.boolean.opBoolean","SPLIT",EDGE,{"disambiguationData":[TD([makeQuery(id+"F1.opExtrude","SWEPT_FACE",FACE,{"disambiguationData":[OSD([sQuery(id+"F0.wireOp",EDGE,"E11.0")])]})])],"derivedFrom":makeQuery(id+"F4.opExtrude","CAP_EDGE",EDGE,{"disambiguationData":[OSD([subQ0])],"isStart":false})});}
            var Q36;
            {var subQ0=sQuery(id+"F3.wireOp",EDGE,"E47");Q36=makeQuery(id+"F4.boolean.opBoolean","SPLIT",EDGE,{"disambiguationData":[TD([makeQuery(id+"F1.opExtrude","SWEPT_FACE",FACE,{"disambiguationData":[OSD([sQuery(id+"F0.wireOp",EDGE,"E11.0")])]})])],"derivedFrom":makeQuery(id+"F4.opExtrude","CAP_EDGE",EDGE,{"disambiguationData":[OSD([subQ0])],"isStart":true})});}
            var Q37;
            {var subQ0=sQuery(id+"F3.wireOp",EDGE,"E46");Q37=makeQuery(id+"F4.boolean.opBoolean","SPLIT",EDGE,{"disambiguationData":[TD([makeQuery(id+"F1.opExtrude","SWEPT_FACE",FACE,{"disambiguationData":[OSD([sQuery(id+"F0.wireOp",EDGE,"E11.0")])]})])],"derivedFrom":makeQuery(id+"F4.opExtrude","CAP_EDGE",EDGE,{"disambiguationData":[OSD([subQ0])],"isStart":false})});}
            var Q38;
            {var subQ0=sQuery(id+"F3.wireOp",EDGE,"E46");Q38=makeQuery(id+"F4.boolean.opBoolean","SPLIT",EDGE,{"disambiguationData":[TD([makeQuery(id+"F1.opExtrude","SWEPT_FACE",FACE,{"disambiguationData":[OSD([sQuery(id+"F0.wireOp",EDGE,"E11.0")])]})])],"derivedFrom":makeQuery(id+"F4.opExtrude","CAP_EDGE",EDGE,{"disambiguationData":[OSD([subQ0])],"isStart":true})});}
            var Q39;
            {var subQ0=sQuery(id+"F3.wireOp",EDGE,"E39");Q39=makeQuery(id+"F4.boolean.opBoolean","SPLIT",EDGE,{"disambiguationData":[TD([makeQuery(id+"F1.opExtrude","SWEPT_FACE",FACE,{"disambiguationData":[OSD([sQuery(id+"F0.wireOp",EDGE,"E10")])]})])],"derivedFrom":makeQuery(id+"F4.opExtrude","CAP_EDGE",EDGE,{"disambiguationData":[OSD([subQ0])],"isStart":false})});}
            fillet(context, id + "F5", {"entities" : qUnion([Q0, Q1, Q2, Q3, Q4, Q5, Q6, Q7, Q8, Q9, Q10, Q11, Q12, Q13, Q14, Q15, Q16, Q17, Q18, Q19, Q20, Q21, Q22, Q23, Q24, Q25, Q26, Q27, Q28, Q29, Q30, Q31, Q32, Q33, Q34, Q35, Q36, Q37, Q38, Q39]), "radius" : 6 * mm, "tangentPropagation" : true, "allowEdgeOverflow" : false});
        }
    });
